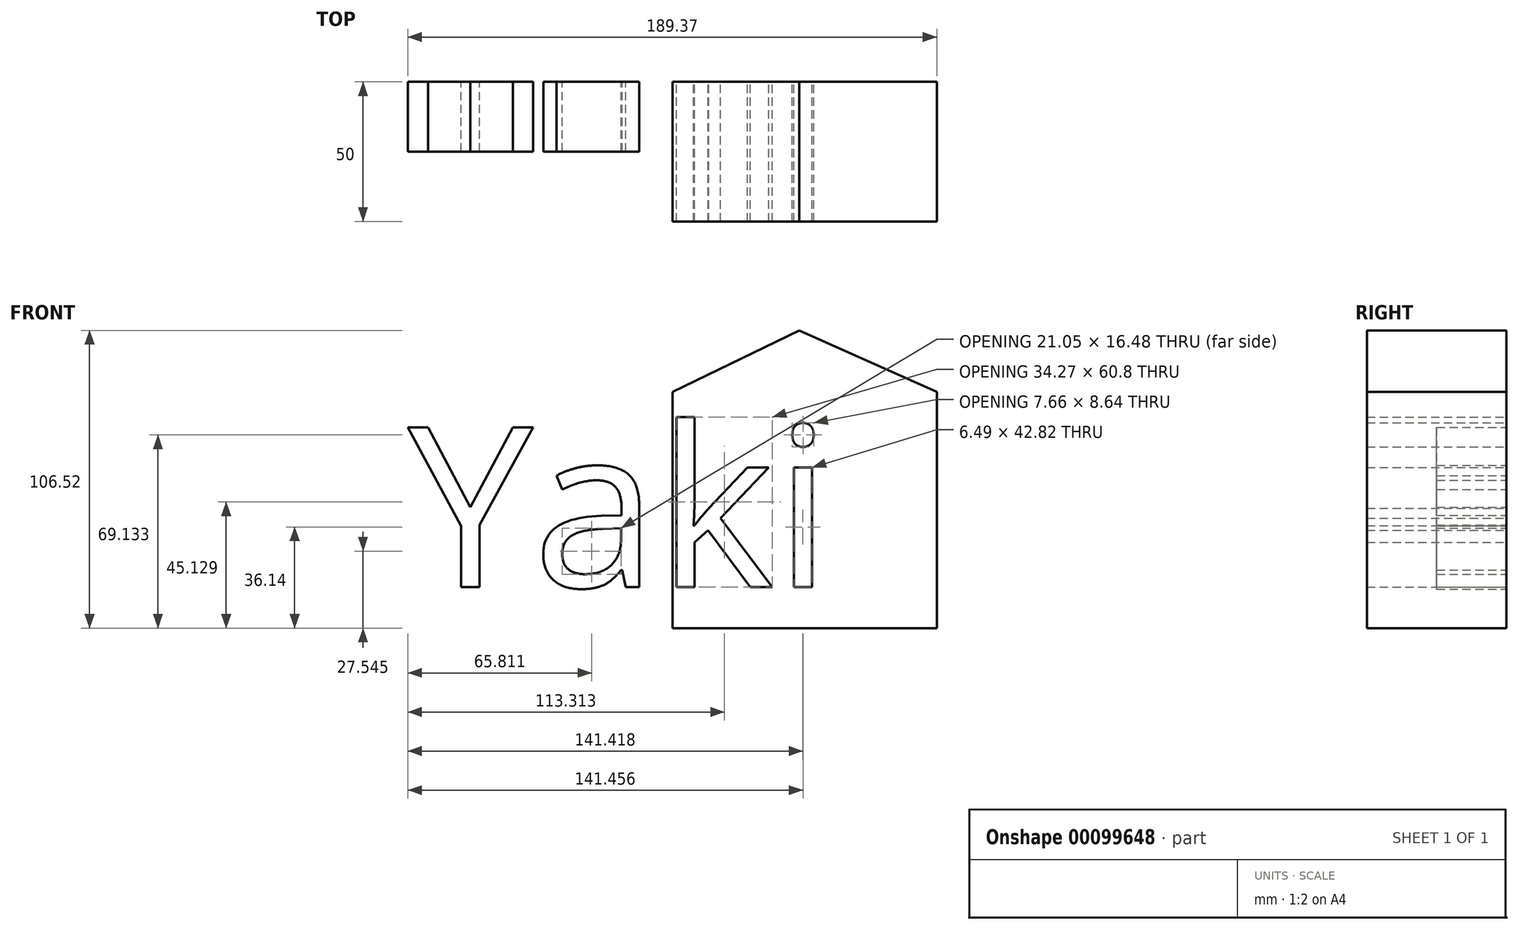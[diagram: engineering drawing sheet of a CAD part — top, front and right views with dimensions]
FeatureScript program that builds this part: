
annotation { "Feature Type Name" : "Feature", "Feature Type Description" : "" }
export const myFeature = defineFeature(function(context is Context, id is Id, definition is map)
    precondition{}
    {
        {
            var Q0;
            Q0=qCreatedBy(makeId("Front.planeOp"),FACE);
            var sketch = newSketch(context, id + "F0", { "sketchPlane" : qUnion([Q0])});
            skLineSegment(sketch, "E0.bottom", {"start": v(-53.84, 53.86) * mm, "end": v(40.77, 53.86) * mm});
            skLineSegment(sketch, "E0.top", {"start": v(-53.84, -30.63) * mm, "end": v(40.77, -30.63) * mm});
            skLineSegment(sketch, "E0.left", {"start": v(-53.84, 53.86) * mm, "end": v(-53.84, -30.63) * mm});
            skLineSegment(sketch, "E0.right", {"start": v(40.77, 53.86) * mm, "end": v(40.77, -30.63) * mm});
            skLineSegment(sketch, "E1", {"start": v(-53.84, 53.86) * mm, "end": v(-8.48, 75.9) * mm});
            skLineSegment(sketch, "E2", {"start": v(-8.48, 75.9) * mm, "end": v(40.77, 53.86) * mm});
            skSolve(sketch);
        }
        {
            var Q0;
            Q0=makeQuery(id+"F0.imprint","IMPRINT",FACE,{"disambiguationData":[TD([[makeQuery(id+"F0.imprint","IMPRINT",EDGE,{"derivedFrom":sQuery(id+"F0.wireOp",EDGE,"E0.bottom")}),-1.0]])]});
            var Q1;
            Q1=makeQuery(id+"F0.imprint","IMPRINT",FACE,{"disambiguationData":[TD([[makeQuery(id+"F0.imprint","IMPRINT",EDGE,{"derivedFrom":sQuery(id+"F0.wireOp",EDGE,"E0.bottom")}),1.0]])]});
            extrude(context, id + "F1", {"entities" : qUnion([Q0, Q1]), "depth" : 50 * mm});
        }
        {
            var Q0;
            Q0=qCreatedBy(makeId("Front.planeOp"),FACE);
            var sketch = newSketch(context, id + "F2", { "sketchPlane" : qUnion([Q0])});
            skText(sketch, "E3", { "text": "Yaki\n\n", "fontName": "OpenSans-Regular.ttf"});
            const initialGuessF2  = {"E3": [-0.1486, -0.0159, 1, 0, 0.05761]};
            skSetInitialGuess(sketch, initialGuessF2);
            skSolve(sketch);
        }
        {
            var Q0;
            Q0=makeQuery(id+"F2.imprint","IMPRINT",FACE,{"disambiguationData":[TD([[makeQuery(id+"F2.imprint","IMPRINT",EDGE,{"derivedFrom":sQuery(id+"F2.wireOp",EDGE,"E3.sketch_text.stroke-0")}),-1.0]])]});
            var Q1;
            Q1=makeQuery(id+"F2.imprint","IMPRINT",FACE,{"disambiguationData":[TD([[makeQuery(id+"F2.imprint","IMPRINT",EDGE,{"derivedFrom":sQuery(id+"F2.wireOp",EDGE,"E3.sketch_text.stroke-9")}),-1.0]])]});
            extrude(context, id + "F3", {"entities" : qUnion([Q0, Q1]), "depth" : 25 * mm});
        }
        {
            var Q0;
            Q0=makeQuery(id+"F2.imprint","IMPRINT",FACE,{"disambiguationData":[TD([[makeQuery(id+"F2.imprint","IMPRINT",EDGE,{"derivedFrom":sQuery(id+"F2.wireOp",EDGE,"E3.sketch_text.stroke-51")}),-1.0]])]});
            var Q1;
            Q1=makeQuery(id+"F2.imprint","IMPRINT",FACE,{"disambiguationData":[TD([[makeQuery(id+"F2.imprint","IMPRINT",EDGE,{"derivedFrom":sQuery(id+"F2.wireOp",EDGE,"E3.sketch_text.stroke-55")}),-1.0]])]});
            var Q2;
            Q2=makeQuery(id+"F2.imprint","IMPRINT",FACE,{"disambiguationData":[TD([[makeQuery(id+"F2.imprint","IMPRINT",EDGE,{"derivedFrom":sQuery(id+"F2.wireOp",EDGE,"E3.sketch_text.stroke-36")}),-1.0]])]});
            extrude(context, id + "F4", {"entities" : qUnion([Q0, Q1, Q2]), "operationType" : NewBodyOperationType.REMOVE, "endBound" : BoundingType.THROUGH_ALL, "depth" : 25 * mm});
        }
    });
